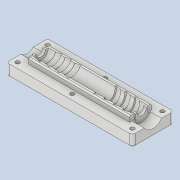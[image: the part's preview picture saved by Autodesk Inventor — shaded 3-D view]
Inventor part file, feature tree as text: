
AUTODESK INVENTOR PART (.ipt)
format: ipt  version: 2020.4 (Build 244396000, 396)  size: 508,416 bytes
history: native  units: mm
features: sketch x13, extrude x12, projected_geometry x9, fillet x2, other x1, mirror x1, boolean_combine x1, chamfer x1
ambient origin geometry x8: Origin, YZ Plane, XZ Plane, XY Plane, X Axis, Y Axis, Z Axis, Center Point
bodies: Volumenkörper1 (feature_tree), Solid2 (feature_tree), Solid3 (feature_tree)
feature tree (40):
  extrude  "Extrusion1"  Depth=6.0mm
  other  "Spirale1"
  mirror  "Spiegeln1"
  extrude  "Extrusion5"  Depth=4.0mm
  extrude  "Extrusion6"  Depth=1.0mm
  boolean_combine  "Combine1"
  extrude  "Extrusion7"  Depth=10.0mm TaperAngle=0.0deg
  extrude  "Extrusion8"  Depth=100.0mm TaperAngle=0.0deg
  extrude  "Extrusion9"  Depth=24.0mm
  extrude  "Extrusion10"  Depth=12.0mm TaperAngle=0.0deg
  extrude  "Extrusion11"  Depth=16.0mm
  chamfer  "Chamfer2"  Distance=4.0mm
  extrude  "Extrusion12"  Depth=3.0mm
  fillet  "Fillet1"  Radius=3.0mm
  extrude  "Extrusion13"  Depth=4.0mm
  fillet  "Fillet2"  Radius=4.0mm
  extrude  "Extrusion14"  Depth=4.0mm
  extrude  "Extrusion15"  Depth=4.0mm
  sketch  "Skizze1"  dims[d0=6.0mm d1=11.0mm]
  sketch  "Skizze3"  dims[d2=36.0mm d3=0.0mm]
  projected_geometry  "Projizierte Kontur2"
  sketch  "Sketch7"  dims[d8=7.0mm d9=24.5mm d10=10.0mm d11=0.0mm d12=90.0deg d13=90.0deg d14=0.0mm d15=0.0mm d16=4.0mm]
  sketch  "Sketch8"  dims[d17=13.962634mm d18=1.0mm]
  sketch  "Sketch9"  dims[d19=0.1mm d32=10.0mm d33=0.0mm]
  projected_geometry  "Projected Loop4"
  sketch  "Sketch10"  dims[d34=7.0mm d35=100.0mm d36=0.0mm]
  projected_geometry  "Projected Loop5"
  projected_geometry  "Projected Loop6"
  projected_geometry  "Projected Loop7"
  projected_geometry  "Projected Loop8"
  sketch  "Sketch11"  dims[d37=82.0mm d38=0.0mm d39=24.0mm]
  projected_geometry  "Projected Loop9"
  sketch  "Sketch12"  dims[d40=30.0mm d41=12.0mm d42=0.0mm]
  sketch  "Sketch13"  dims[d43=74.0mm d44=16.0mm]
  projected_geometry  "Projected Loop10"
  projected_geometry  "Projected Loop11"
  sketch  "Sketch14"  dims[d45=79.0mm]
  sketch  "Sketch15"  dims[d46=21.0mm d47=4.0mm d48=0.0mm]
  sketch  "Sketch16"  dims[d49=3.0mm d50=3.0mm d51=3.0mm]
  sketch  "Sketch17"  dims[d52=3.0mm d53=4.0mm d54=4.0mm d55=4.0mm d56=4.0mm d57=4.0mm d58=4.0mm d59=4.0mm d60=4.0mm d61=10.0mm d62=0.0mm d63=1.0mm d64=1.0mm d65=1.0mm d66=1.0mm d67=6.0mm d68=10.0mm d69=0.0mm d70=10.0mm d71=0.0mm d72=1.0mm d73=2.0mm d74=45.0deg d75=3.0mm d76=3.0mm d77=4.0mm d78=46.0mm d79=4.0mm d80=44.0mm d81=5.5mm d82=5.5mm d83=5.5mm d84=5.5mm d85=5.5mm d86=5.5mm d87=5.0mm d88=0.0mm d89=2.0mm d90=0.5mm d91=6.5mm d92=74.1mm d93=2.1mm d94=0.0mm d95=0.0mm d96=1.0mm d97=12.0mm d98=0.2mm d99=7.9mm d100=0.0mm d101=0.0mm d102=15.0mm d103=0.2mm d104=7.9mm d105=0.0mm d106=0.0mm]
